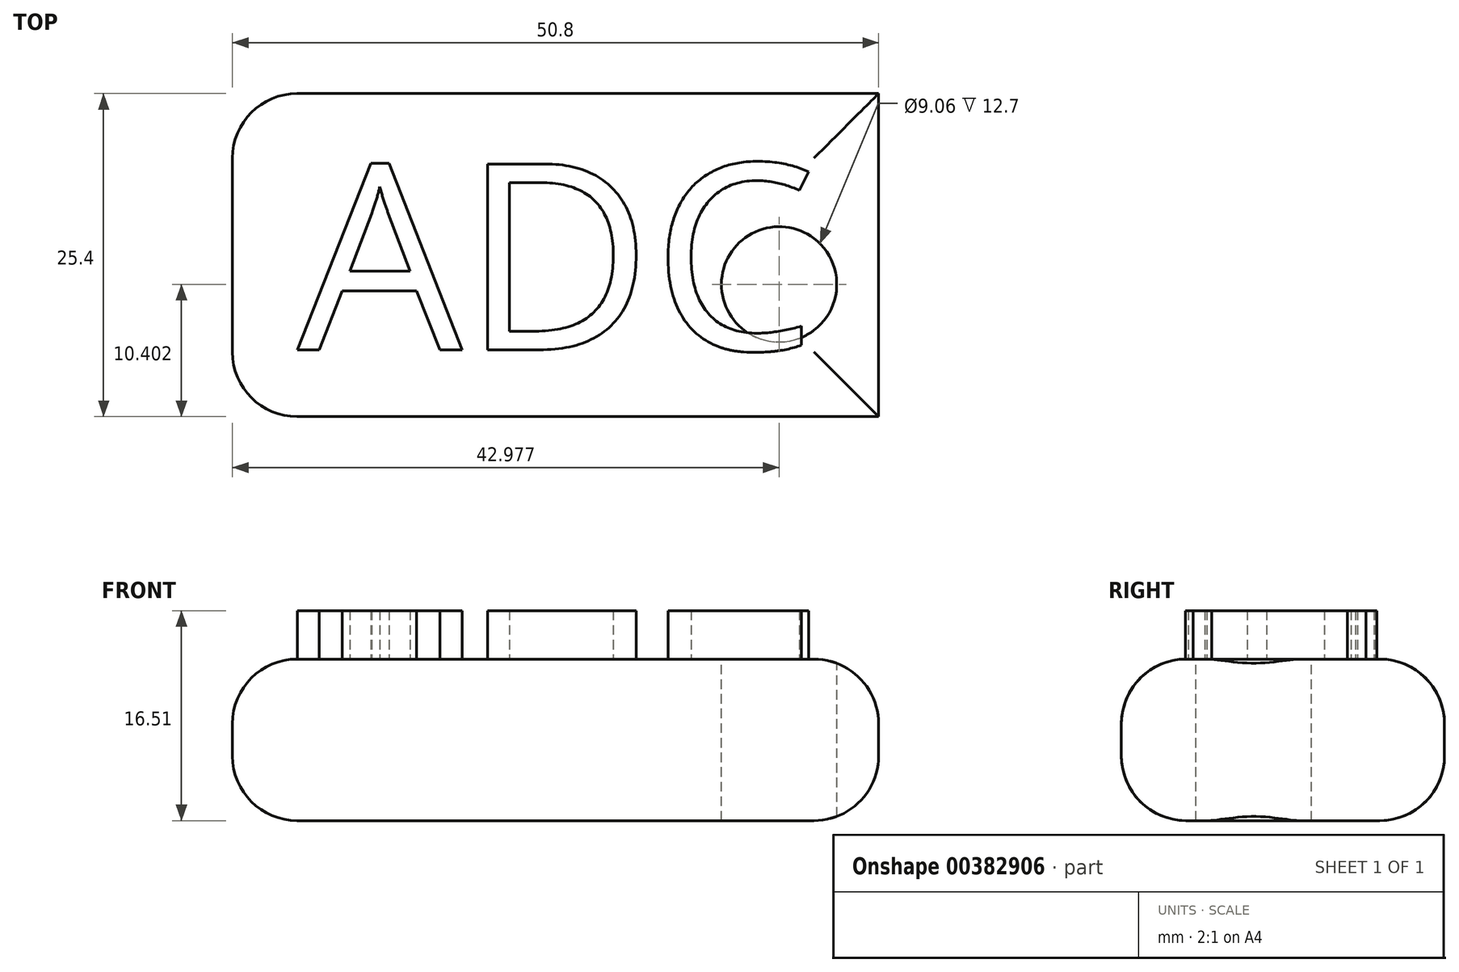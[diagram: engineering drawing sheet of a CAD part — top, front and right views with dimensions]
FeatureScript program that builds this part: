
annotation { "Feature Type Name" : "Feature", "Feature Type Description" : "" }
export const myFeature = defineFeature(function(context is Context, id is Id, definition is map)
    precondition{}
    {
        {
            var Q0;
            Q0=qCreatedBy(makeId("Top.planeOp"),FACE);
            var sketch = newSketch(context, id + "F0", { "sketchPlane" : qUnion([Q0])});
            skLineSegment(sketch, "E0.bottom", {"start": v(0, 0) * mm, "end": v(50.8, 0) * mm});
            skLineSegment(sketch, "E0.top", {"start": v(0, -25.4) * mm, "end": v(50.8, -25.4) * mm});
            skLineSegment(sketch, "E0.left", {"start": v(0, 0) * mm, "end": v(0, -25.4) * mm});
            skLineSegment(sketch, "E0.right", {"start": v(50.8, 0) * mm, "end": v(50.8, -25.4) * mm});
            skSolve(sketch);
        }
        {
            var Q0;
            Q0=makeQuery(id+"F0.imprint","IMPRINT",FACE,{"disambiguationData":[TD([[makeQuery(id+"F0.imprint","IMPRINT",EDGE,{"derivedFrom":sQuery(id+"F0.wireOp",EDGE,"E0.bottom")}),-1.0]])]});
            extrude(context, id + "F1", {"entities" : qUnion([Q0]), "depth" : 12.7 * mm});
        }
        {
            var Q0;
            Q0=makeQuery(id+"F1.opExtrude","CAP_FACE",FACE,{"disambiguationData":[OSD([sQuery(id+"F0.wireOp",EDGE,"E0.bottom"),sQuery(id+"F0.wireOp",EDGE,"E0.top"),sQuery(id+"F0.wireOp",EDGE,"E0.left"),sQuery(id+"F0.wireOp",EDGE,"E0.right")])],"isStart":false});
            var sketch = newSketch(context, id + "F2", { "sketchPlane" : qUnion([Q0])});
            skCircle(sketch, "E1", {"center": v(42.98, -15) * mm, "radius": 4.53 * mm});
            skSolve(sketch);
        }
        {
            var Q0;
            Q0 = qSketchRegion(id + "F2", true);
            extrude(context, id + "F3", {"entities" : qUnion([Q0]), "operationType" : NewBodyOperationType.REMOVE, "oppositeDirection" : true, "depth" : 25.4 * mm});
        }
        {
            var Q0;
            Q0=makeQuery(id+"F1.opExtrude","CAP_FACE",FACE,{"disambiguationData":[OSD([sQuery(id+"F0.wireOp",EDGE,"E0.bottom"),sQuery(id+"F0.wireOp",EDGE,"E0.top"),sQuery(id+"F0.wireOp",EDGE,"E0.left"),sQuery(id+"F0.wireOp",EDGE,"E0.right")])],"isStart":false});
            var sketch = newSketch(context, id + "F4", { "sketchPlane" : qUnion([Q0])});
            skSolve(sketch);
        }
        {
            var Q0;
            Q0=makeQuery(id+"F1.opExtrude","CAP_EDGE",EDGE,{"disambiguationData":[OSD([sQuery(id+"F0.wireOp",EDGE,"E0.top")])],"isStart":false});
            var Q1;
            Q1=makeQuery(id+"F1.opExtrude","CAP_EDGE",EDGE,{"disambiguationData":[OSD([sQuery(id+"F0.wireOp",EDGE,"E0.right")])],"isStart":false});
            var Q2;
            Q2=makeQuery(id+"F1.opExtrude","CAP_EDGE",EDGE,{"disambiguationData":[OSD([sQuery(id+"F0.wireOp",EDGE,"E0.right")])],"isStart":true});
            var Q3;
            Q3=makeQuery(id+"F1.opExtrude","CAP_EDGE",EDGE,{"disambiguationData":[OSD([sQuery(id+"F0.wireOp",EDGE,"E0.top")])],"isStart":true});
            var Q4;
            Q4=makeQuery(id+"F1.opExtrude","CAP_EDGE",EDGE,{"disambiguationData":[OSD([sQuery(id+"F0.wireOp",EDGE,"E0.bottom")])],"isStart":true});
            var Q5;
            Q5=makeQuery(id+"F1.opExtrude","CAP_EDGE",EDGE,{"disambiguationData":[OSD([sQuery(id+"F0.wireOp",EDGE,"E0.bottom")])],"isStart":false});
            var Q6;
            Q6=makeQuery(id+"F1.opExtrude","SWEPT_EDGE",EDGE,{"disambiguationData":[OSD([sQuery(id+"F0.wireOp",EDGE,"E0.bottom"),sQuery(id+"F0.wireOp",EDGE,"E0.left")])]});
            var Q7;
            Q7=makeQuery(id+"F1.opExtrude","CAP_EDGE",EDGE,{"disambiguationData":[OSD([sQuery(id+"F0.wireOp",EDGE,"E0.left")])],"isStart":false});
            var Q8;
            Q8=makeQuery(id+"F1.opExtrude","CAP_EDGE",EDGE,{"disambiguationData":[OSD([sQuery(id+"F0.wireOp",EDGE,"E0.left")])],"isStart":true});
            var Q9;
            Q9=makeQuery(id+"F1.opExtrude","SWEPT_EDGE",EDGE,{"disambiguationData":[OSD([sQuery(id+"F0.wireOp",EDGE,"E0.top"),sQuery(id+"F0.wireOp",EDGE,"E0.left")])]});
            fillet(context, id + "F5", {"entities" : qUnion([Q0, Q1, Q2, Q3, Q4, Q5, Q6, Q7, Q8, Q9]), "radius" : 5.08 * mm, "tangentPropagation" : true, "allowEdgeOverflow" : false});
        }
        {
            var Q0;
            Q0=makeQuery(id+"F4.imprint","IMPRINT",FACE,{"disambiguationData":[TD([[makeQuery(id+"F4.imprint","IMPRINT",EDGE,{"derivedFrom":makeQuery(id+"F1.opExtrude","CAP_EDGE",EDGE,{"disambiguationData":[OSD([sQuery(id+"F0.wireOp",EDGE,"E0.bottom")])],"isStart":false})}),-1.0]])]});
            var sketch = newSketch(context, id + "F6", { "sketchPlane" : qUnion([Q0])});
            skText(sketch, "E2", { "text": "ADC", "fontName": "OpenSans-Regular.ttf"});
            const initialGuessF6  = {"E2": [0.00511, -0.02015, 1, 0, 0.01474]};
            skSetInitialGuess(sketch, initialGuessF6);
            skSolve(sketch);
        }
        {
            var Q0;
            Q0 = qSketchRegion(id + "F6", true);
            extrude(context, id + "F7", {"entities" : qUnion([Q0]), "operationType" : NewBodyOperationType.ADD, "depth" : 3.8 * mm});
        }
    });
